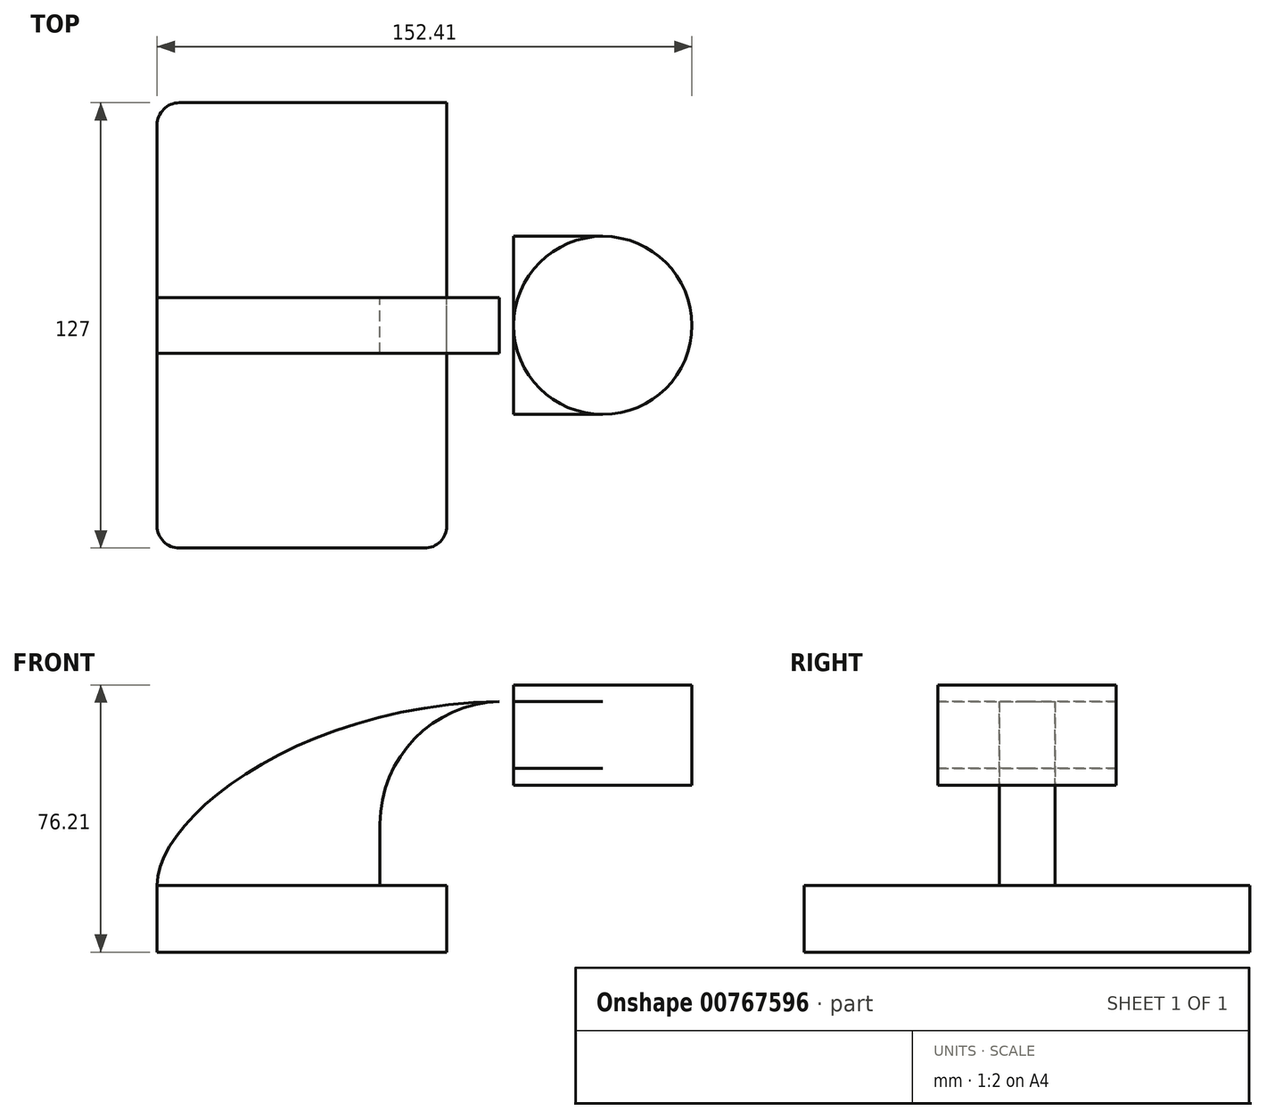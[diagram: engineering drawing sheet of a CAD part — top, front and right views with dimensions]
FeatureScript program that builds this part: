
annotation { "Feature Type Name" : "Feature", "Feature Type Description" : "" }
export const myFeature = defineFeature(function(context is Context, id is Id, definition is map)
    precondition{}
    {
        {
            var Q0;
            Q0=qCreatedBy(makeId("Front.planeOp"),FACE);
            var sketch = newSketch(context, id + "F0", { "sketchPlane" : qUnion([Q0])});
            skLineSegment(sketch, "E0.bottom", {"start": v(-41.27, -9.53) * mm, "end": v(41.28, -9.53) * mm});
            skLineSegment(sketch, "E0.top", {"start": v(-41.28, 9.53) * mm, "end": v(41.27, 9.53) * mm});
            skLineSegment(sketch, "E0.left", {"start": v(-41.28, -9.53) * mm, "end": v(-41.28, 9.53) * mm});
            skLineSegment(sketch, "E0.right", {"start": v(41.28, -9.53) * mm, "end": v(41.28, 9.53) * mm});
            skPoint(sketch, "E0.middle", {"position": v(0, 0) * mm});
            skLineSegment(sketch, "E1.bottom", {"start": v(60.32, 66.67) * mm, "end": v(111.13, 66.67) * mm});
            skLineSegment(sketch, "E1.top", {"start": v(60.32, 38.1) * mm, "end": v(111.12, 38.1) * mm});
            skLineSegment(sketch, "E1.left", {"start": v(60.32, 66.68) * mm, "end": v(60.32, 38.1) * mm});
            skLineSegment(sketch, "E1.right", {"start": v(111.12, 66.68) * mm, "end": v(111.12, 38.1) * mm});
            skPoint(sketch, "E1.middle", {"position": v(85.72, 52.39) * mm});
            skArc(sketch, "E2", {"start": v(41.27, 27) * mm, "mid": v(45.92, 38.23) * mm, "end": v(57.15, 42.88) * mm});
            skLineSegment(sketch, "E3", {"start": v(57.15, 42.88) * mm, "end": v(85.72, 42.88) * mm});
            skLineSegment(sketch, "E4", {"start": v(41.27, 9.53) * mm, "end": v(41.27, 27) * mm});
            skLineSegment(sketch, "E5.0", {"start": v(57.15, 61.93) * mm, "end": v(85.72, 61.93) * mm});
            skArc(sketch, "E5.1", {"start": v(22.22, 27) * mm, "mid": v(32.45, 51.7) * mm, "end": v(57.15, 61.93) * mm});
            skLineSegment(sketch, "E5.2", {"start": v(22.23, 9.52) * mm, "end": v(22.22, 27) * mm});
            skLineSegment(sketch, "E6", {"start": v(85.72, 38.1) * mm, "end": v(85.72, 66.67) * mm});
            skFitSpline(sketch, "E7", {"points": [v(-41.28, 9.53) * mm, v(57.15, 61.93) * mm], "startDerivative": vector(-0.17, 58.73) * mm, "endDerivative": vector(171.45, 1.77) * mm});
            skSolve(sketch);
        }
        {
            var Q0;
            Q0=makeQuery(id+"F0.imprint","IMPRINT",FACE,{"disambiguationData":[TD([[makeQuery(id+"F0.imprint","IMPRINT",EDGE,{"derivedFrom":sQuery(id+"F0.wireOp",EDGE,"E0.bottom")}),1.0]])]});
            extrude(context, id + "F1", {"entities" : qUnion([Q0]), "endBound" : BoundingType.SYMMETRIC, "depth" : 127 * mm, "offsetDistance" : 25.4 * mm});
        }
        {
            var Q0;
            {var subQ1=sQuery(id+"F0.wireOp",EDGE,"E2");Q0=makeQuery(id+"F0.imprint","IMPRINT",FACE,{"disambiguationData":[TD([[makeQuery(id+"F0.imprint","IMPRINT",EDGE,{"derivedFrom":subQ1}),1.0]])]});}
            var Q1;
            {var subQ0=sQuery(id+"F0.wireOp",EDGE,"E5.0");var subQ1=sQuery(id+"F0.wireOp",EDGE,"E1.left");var subQ2=makeQuery(id+"F0.imprint","INTERSECT",VERTEX,{"derivedFrom":[subQ1,subQ0]});Q1=makeQuery(id+"F0.imprint","IMPRINT",FACE,{"disambiguationData":[TD([[makeQuery(id+"F0.imprint","IMPRINT",EDGE,{"disambiguationData":[TD([[subQ2,-1.0]])],"derivedFrom":subQ1}),1.0]])]});}
            extrude(context, id + "F2", {"entities" : qUnion([Q0, Q1]), "operationType" : NewBodyOperationType.ADD, "endBound" : BoundingType.SYMMETRIC, "depth" : 50.8 * mm, "offsetDistance" : 25.4 * mm});
        }
        {
            var Q0;
            {var subQ3=sQuery(id+"F0.wireOp",EDGE,"E5.2");Q0=makeQuery(id+"F0.imprint","IMPRINT",FACE,{"disambiguationData":[TD([[makeQuery(id+"F0.imprint","IMPRINT",EDGE,{"derivedFrom":subQ3}),1.0]])]});}
            extrude(context, id + "F3", {"entities" : qUnion([Q0]), "operationType" : NewBodyOperationType.ADD, "endBound" : BoundingType.SYMMETRIC, "depth" : 15.88 * mm, "offsetDistance" : 25.4 * mm});
        }
        {
            var Q0;
            {var subQ4=sQuery(id+"F0.wireOp",EDGE,"E1.right");Q0=makeQuery(id+"F0.imprint","IMPRINT",FACE,{"disambiguationData":[TD([[makeQuery(id+"F0.imprint","IMPRINT",EDGE,{"derivedFrom":subQ4}),-1.0]])]});}
            var Q1;
            Q1=sQuery(id+"F0.wireOp",EDGE,"E6");
            revolve(context, id + "F4", {"operationType" : NewBodyOperationType.ADD, "surfaceOperationType" : NewSurfaceOperationType.NEW, "entities" : qUnion([Q0]), "axis" : qUnion([Q1]), "revolveType" : RevolveType.FULL});
        }
        {
            var Q0;
            Q0=makeQuery(id+"F1.opExtrude","CAP_EDGE",EDGE,{"disambiguationData":[OSD([sQuery(id+"F0.wireOp",EDGE,"E0.right")])],"isStart":false});
            var Q1;
            Q1=makeQuery(id+"F1.opExtrude","CAP_EDGE",EDGE,{"disambiguationData":[OSD([sQuery(id+"F0.wireOp",EDGE,"E0.left")])],"isStart":false});
            var Q2;
            Q2=makeQuery(id+"F1.opExtrude","CAP_EDGE",EDGE,{"disambiguationData":[OSD([sQuery(id+"F0.wireOp",EDGE,"E0.left")])],"isStart":true});
            fillet(context, id + "F5", {"entities" : qUnion([Q0, Q1, Q2]), "radius" : 6.35 * mm, "tangentPropagation" : true, "allowEdgeOverflow" : false});
        }
    });
